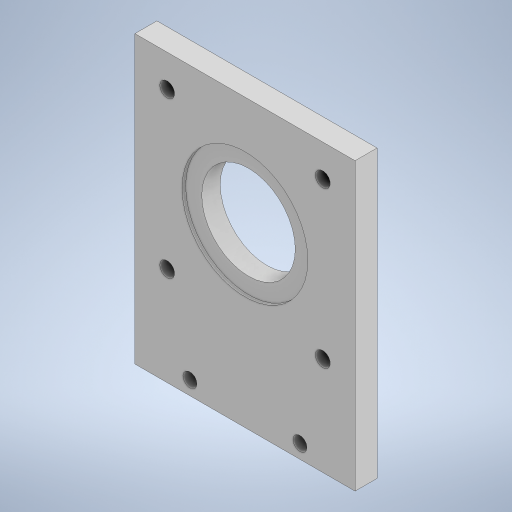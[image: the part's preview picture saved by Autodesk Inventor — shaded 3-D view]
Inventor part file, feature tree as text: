
AUTODESK INVENTOR PART (.ipt)
format: ipt  version: 2024 (Build 280153000, 153)  size: 272,896 bytes
history: native  units: in
note: dims shown in document units (in); Inventor stores cm internally (conversion verified against a paired STEP export)
features: extrude x4, sketch x4
ambient origin geometry x8: Origin, YZ Plane, XZ Plane, XY Plane, X Axis, Y Axis, Z Axis, Center Point
bodies: Solid1 (feature_tree)
feature tree (8):
  extrude  "Extrusion1"  Depth=10.2362in
  extrude  "Extrusion2"  Depth=0.7874in
  extrude  "Extrusion6"  Depth=3.937in
  extrude  "Extrusion11"  Depth=0.126in
  sketch  "Sketch1"  dims[d0=7.874in d1=10.2362in]
  sketch  "Sketch2"  dims[d2=0.7874in d3=0.0in d4=3.3465in]
  sketch  "Sketch6"  dims[d5=3.937in d6=3.937in]
  sketch  "Sketch12"  dims[d7=1.1811in d8=0.0in d18=2.7839in d19=2.7839in d20=2.7839in d21=2.7839in d22=2.7839in d23=2.7839in d24=2.7839in d25=2.7839in d26=0.5315in d27=0.5315in d28=0.5315in d29=0.5315in d30=0.7874in d31=0.0in d57=0.5in d58=0.5in d59=1.969in d60=1.969in d61=0.492in d62=0.492in d66=4.5in d67=0.126in d68=0.0in]
